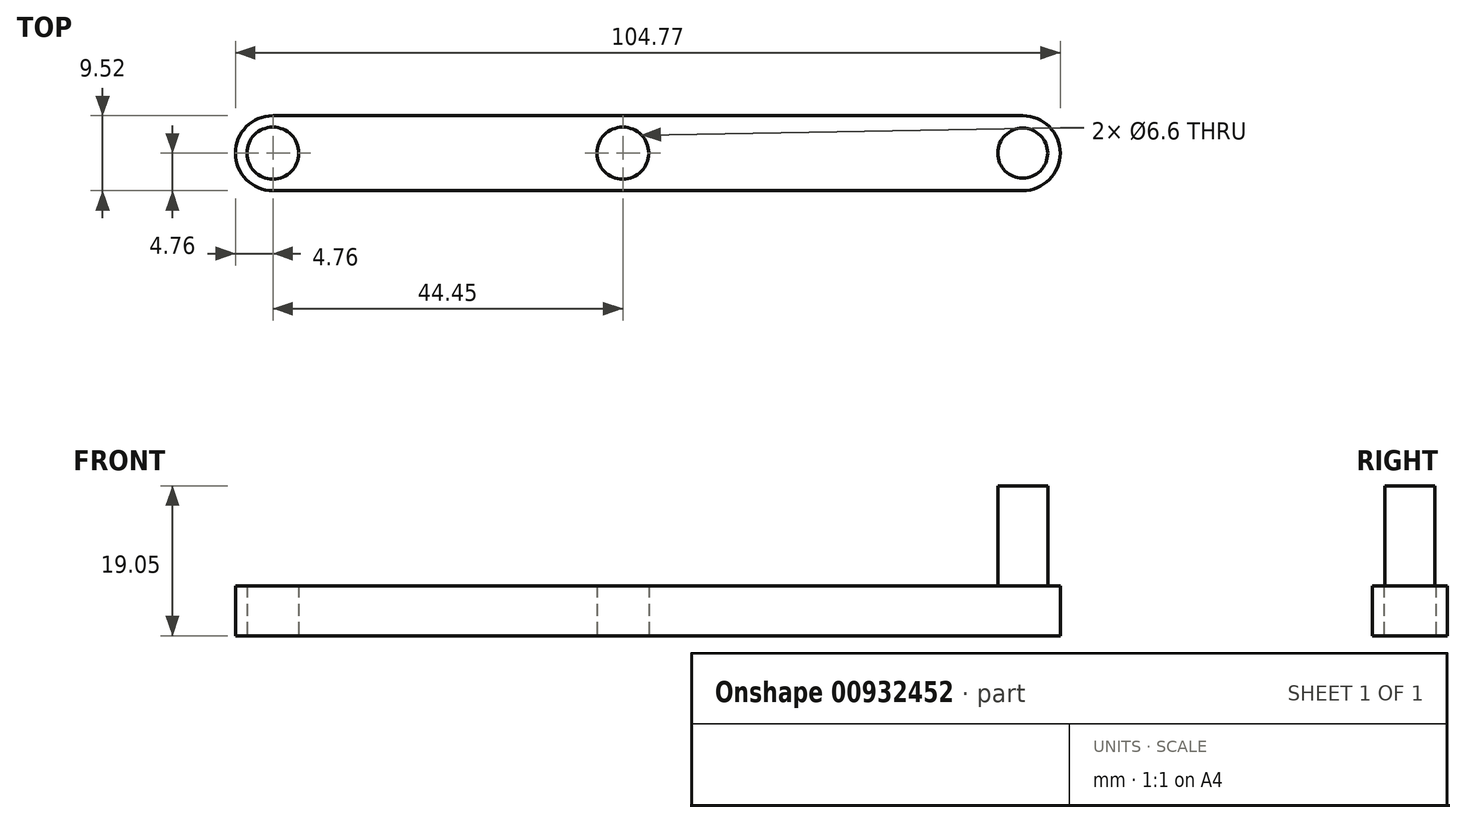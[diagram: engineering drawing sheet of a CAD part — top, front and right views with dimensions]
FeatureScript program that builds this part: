
annotation { "Feature Type Name" : "Feature", "Feature Type Description" : "" }
export const myFeature = defineFeature(function(context is Context, id is Id, definition is map)
    precondition{}
    {
        {
            var Q0;
            Q0=qCreatedBy(makeId("Top.planeOp"),FACE);
            var sketch = newSketch(context, id + "F0", { "sketchPlane" : qUnion([Q0])});
            skLineSegment(sketch, "E0", {"start": v(0, 4.76) * mm, "end": v(-95.25, 4.76) * mm});
            skLineSegment(sketch, "E1", {"start": v(-95.25, -4.76) * mm, "end": v(0, -4.76) * mm});
            skArc(sketch, "E2", {"start": v(0, -4.76) * mm, "mid": v(4.76, 0) * mm, "end": v(0, 4.76) * mm});
            skArc(sketch, "E3", {"start": v(-95.25, -4.76) * mm, "mid": v(-100.01, 0) * mm, "end": v(-95.25, 4.76) * mm});
            skLineSegment(sketch, "E4", {"start": v(-95.25, 0) * mm, "end": v(0, 0) * mm, "construction": true});
            skCircle(sketch, "E5", {"center": v(0, 0) * mm, "radius": 3.18 * mm});
            skCircle(sketch, "E6", {"center": v(-95.25, 0) * mm, "radius": 3.3 * mm});
            skCircle(sketch, "E7", {"center": v(-50.8, 0) * mm, "radius": 3.3 * mm});
            skSolve(sketch);
        }
        {
            var Q0;
            Q0 = qSketchRegion(id + "F0", true);
            extrude(context, id + "F1", {"entities" : qUnion([Q0]), "depth" : 6.35 * mm, "offsetDistance" : 25.4 * mm});
        }
        {
            var Q0;
            Q0=makeQuery(id+"F1.opExtrude","CAP_FACE",FACE,{"disambiguationData":[OSD([sQuery(id+"F0.wireOp",EDGE,"E0"),sQuery(id+"F0.wireOp",EDGE,"E1"),sQuery(id+"F0.wireOp",EDGE,"E2"),sQuery(id+"F0.wireOp",EDGE,"E3"),sQuery(id+"F0.wireOp",EDGE,"E5"),sQuery(id+"F0.wireOp",EDGE,"E6"),sQuery(id+"F0.wireOp",EDGE,"E7")])],"isStart":false});
            var sketch = newSketch(context, id + "F2", { "sketchPlane" : qUnion([Q0])});
            skCircle(sketch, "E8", {"center": v(0, 0) * mm, "radius": 3.18 * mm});
            skSolve(sketch);
        }
        {
            var Q0;
            Q0 = qSketchRegion(id + "F2", true);
            extrude(context, id + "F3", {"entities" : qUnion([Q0]), "operationType" : NewBodyOperationType.ADD, "depth" : 12.7 * mm, "offsetDistance" : 25.4 * mm, "hasSecondDirection" : true, "secondDirectionOppositeDirection" : true, "secondDirectionDepth" : 6.35 * mm});
        }
    });
